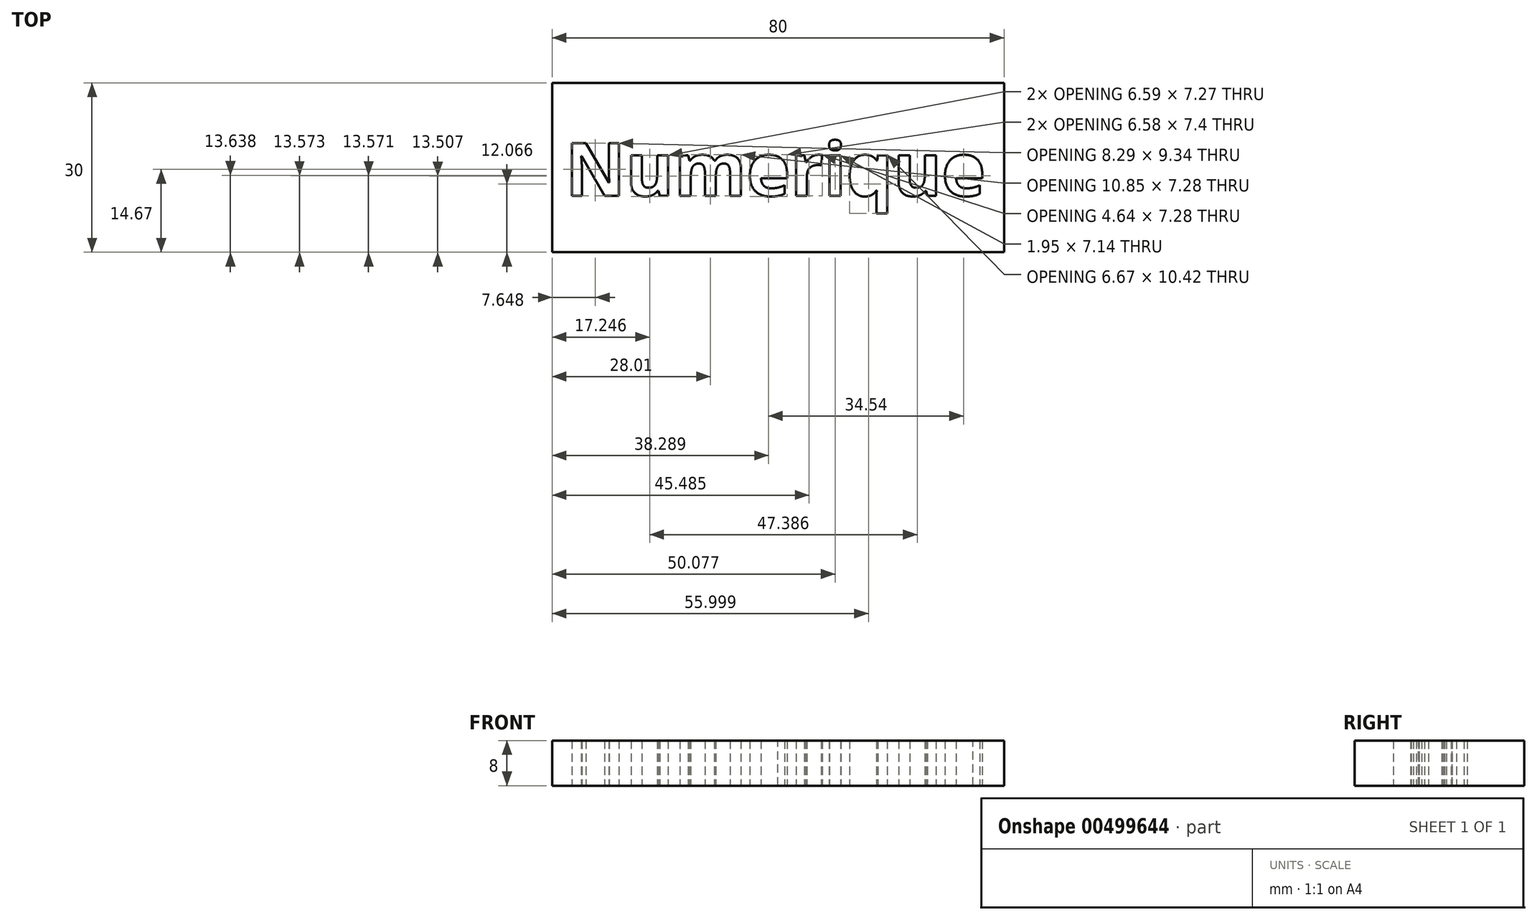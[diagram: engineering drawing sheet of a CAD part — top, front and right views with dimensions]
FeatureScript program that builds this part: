
annotation { "Feature Type Name" : "Feature", "Feature Type Description" : "" }
export const myFeature = defineFeature(function(context is Context, id is Id, definition is map)
    precondition{}
    {
        {
            var Q0;
            Q0=qCreatedBy(makeId("Top.planeOp"),FACE);
            var sketch = newSketch(context, id + "F0", { "sketchPlane" : qUnion([Q0])});
            skLineSegment(sketch, "E0.bottom", {"start": v(-47.85, 9.86) * mm, "end": v(32.15, 9.86) * mm});
            skLineSegment(sketch, "E0.top", {"start": v(-47.85, -20.14) * mm, "end": v(32.15, -20.14) * mm});
            skLineSegment(sketch, "E0.left", {"start": v(-47.85, 9.86) * mm, "end": v(-47.85, -20.14) * mm});
            skLineSegment(sketch, "E0.right", {"start": v(32.15, 9.86) * mm, "end": v(32.15, -20.14) * mm});
            skText(sketch, "E1", { "text": "Numerique", "fontName": "OpenSans-Bold.ttf"});
            const initialGuessF0  = {"E1": [-0.04552, -0.01014, 1, 0, 0.00942]};
            skSetInitialGuess(sketch, initialGuessF0);
            skSolve(sketch);
        }
        {
            var Q0;
            Q0 = qSketchRegion(id + "F0", true);
            extrude(context, id + "F1", {"entities" : qUnion([Q0]), "depth" : 8 * mm});
        }
    });
